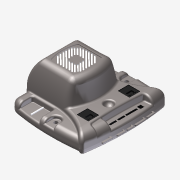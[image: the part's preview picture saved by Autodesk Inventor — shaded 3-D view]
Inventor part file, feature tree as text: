
AUTODESK INVENTOR PART (.ipt)
format: ipt  version: 2013 (Build 170138000, 138)  size: 5,698,048 bytes
history: native  units: mm
features: extrude x8, sketch x6, mirror x3, plane x2, other x2, imported_body x1
ambient origin geometry x8: Origin, YZ Plane, XZ Plane, XY Plane, X Axis, Y Axis, Z Axis, Center Point
bodies: Solid1 (feature_tree)
feature tree (22):
  imported_body  "Base1"
  sketch  "Sketch1"  dims[d50=0.9144mm d57=1.467403mm]
  extrude  "Extrusion2"  Depth=1.467403mm
  plane  "Work Plane1"
  mirror  "Mirror1"
  extrude  "Extrusion3"  Depth=1.467403mm
  sketch  "Sketch2"  dims[d58=1.467403mm d59=1.467403mm]
  extrude  "Extrusion4"  Depth=1.467403mm
  extrude  "Extrusion6"  Depth=1.467403mm
  extrude  "Extrusion7"  TaperAngle=90.0deg  [1 undecoded]
  mirror  "Mirror2"
  extrude  "Extrusion8"  Depth=9.7282mm
  mirror  "Mirror3"
  sketch  "Sketch5"  dims[d62=1.467403mm d63=1.467403mm]
  other  "Work Axis1"
  extrude  "Extrusion9"  Depth=0.762mm TaperAngle=0.0deg
  plane  "Work Plane2"
  extrude  "Extrusion10"  Depth=0.762mm
  sketch  "Sketch4"  dims[d60=1.467403mm d61=1.467403mm]
  sketch  "Sketch6"  dims[d66=1.27mm d67=0.0mm d70=90.0deg]
  sketch  "Sketch7"  dims[d71=1.27mm d72=0.0mm d73=9.7282mm d75=0.762mm d76=0.0mm d77=0.762mm d80=2.54mm d81=0.0mm d82=0.254mm d83=0.0mm d84=1.016mm d85=0.0mm d86=1.27mm d87=2.286mm d88=4.572mm d89=4.572mm d90=3.81mm d91=0.0mm d92=-15.24mm d105=129.575698mm d160=0.254mm d162=1.27mm d169=0.635mm d182=1.27mm d183=0.0mm]
  other  "Image2"
note: 1 required parameter value undecoded (feature->parameter linkage not recoverable at this tier; creation-order binding heuristic only, values carry confidence <= 0.55)
